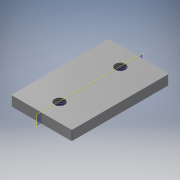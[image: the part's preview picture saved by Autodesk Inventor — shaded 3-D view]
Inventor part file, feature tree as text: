
AUTODESK INVENTOR PART (.ipt)
format: ipt  version: 2017 (Build 210142000, 142)  size: 127,488 bytes
history: native  units: mm
features: plane x2, sheet_metal_op x1, hole x1, mirror x1, chamfer x1, sketch x1, other x1
ambient origin geometry x8: Origin, YZ Plane, XZ Plane, XY Plane, X Axis, Y Axis, Z Axis, Center Point
bodies: Solid1 (feature_tree)
feature tree (8):
  sheet_metal_op  "Face1"
  hole  "Hole1"  [1 undecoded]
  plane  "Work Plane1"
  plane  "Work Plane2"
  mirror  "Mirror1"
  chamfer  "Corner Round1"
  sketch  "Sketch1"  dims[d2=80.0mm d3=50.0mm d4=0.001mm d5=15.0mm d6=25.0mm d7=8.376mm d8=6.0mm d9=4.0mm d10=2.0mm d11=90.0deg d12=8.0mm d13=20.594885mm d14=1.0mm]
  other  "Plate1"
note: 1 required parameter value undecoded (feature->parameter linkage not recoverable at this tier; creation-order binding heuristic only, values carry confidence <= 0.55)
